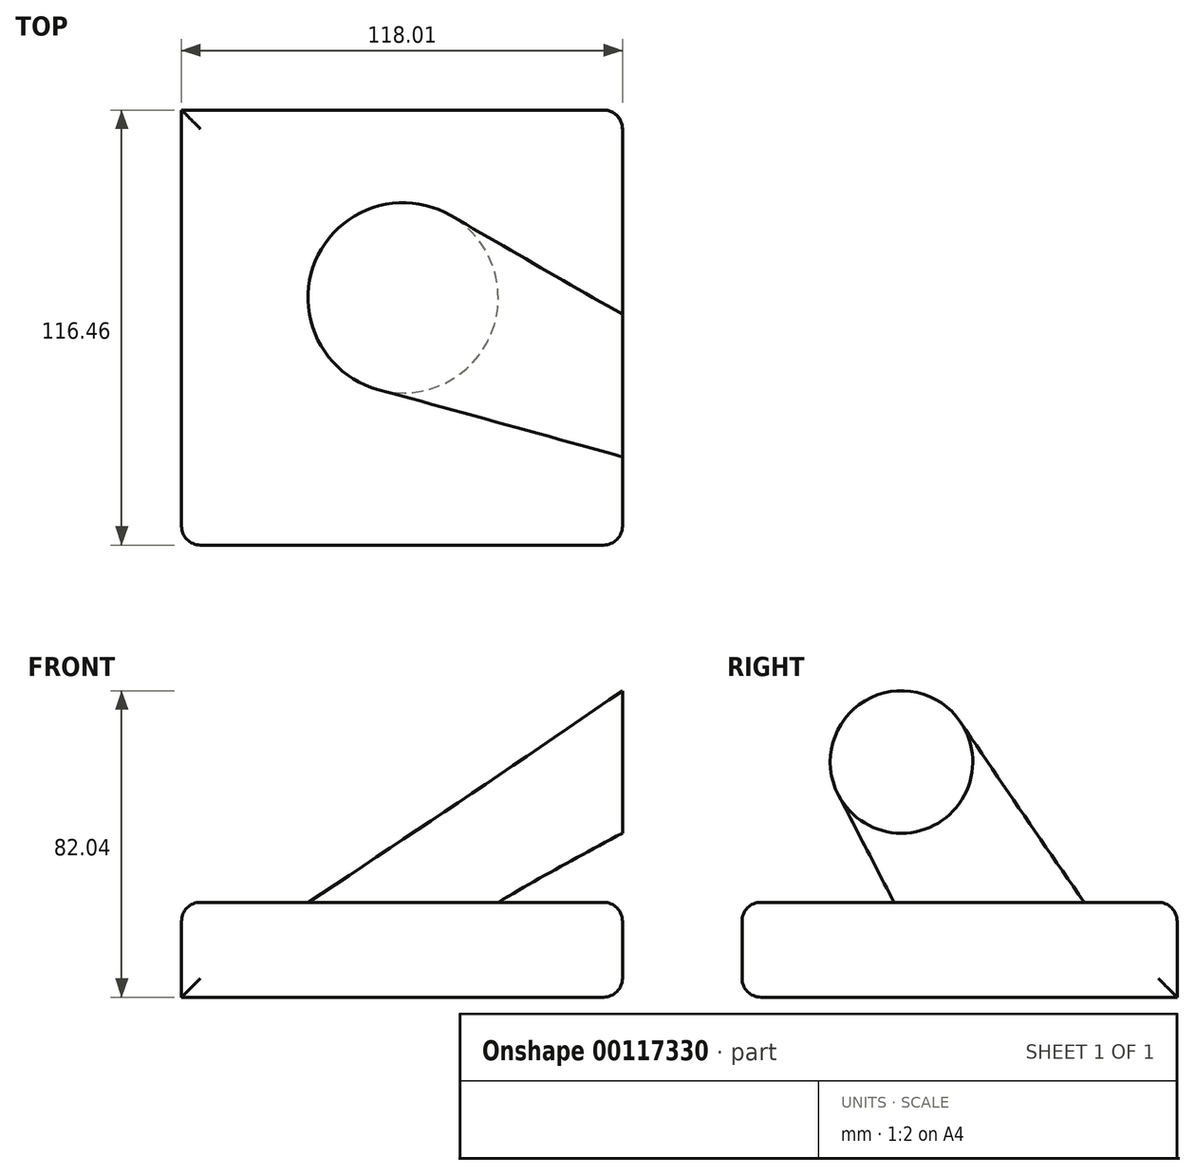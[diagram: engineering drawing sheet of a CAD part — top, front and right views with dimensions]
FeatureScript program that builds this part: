
annotation { "Feature Type Name" : "Feature", "Feature Type Description" : "" }
export const myFeature = defineFeature(function(context is Context, id is Id, definition is map)
    precondition{}
    {
        {
            var Q0;
            Q0=qCreatedBy(makeId("Top.planeOp"),FACE);
            var sketch = newSketch(context, id + "F0", { "sketchPlane" : qUnion([Q0])});
            skLineSegment(sketch, "E0.bottom", {"start": v(-59.31, -66.17) * mm, "end": v(58.7, -66.17) * mm});
            skLineSegment(sketch, "E0.top", {"start": v(-59.31, 50.29) * mm, "end": v(58.7, 50.29) * mm});
            skLineSegment(sketch, "E0.left", {"start": v(-59.31, -66.17) * mm, "end": v(-59.31, 50.29) * mm});
            skLineSegment(sketch, "E0.right", {"start": v(58.7, -66.17) * mm, "end": v(58.7, 50.29) * mm});
            skSolve(sketch);
        }
        {
            var Q0;
            Q0 = qSketchRegion(id + "F0", true);
            extrude(context, id + "F1", {"entities" : qUnion([Q0]), "depth" : 25.4 * mm});
        }
        {
            var Q0;
            Q0=makeQuery(id+"F1.opExtrude","CAP_EDGE",EDGE,{"disambiguationData":[OSD([sQuery(id+"F0.wireOp",EDGE,"E0.bottom")])],"isStart":false});
            var Q1;
            Q1=makeQuery(id+"F1.opExtrude","CAP_EDGE",EDGE,{"disambiguationData":[OSD([sQuery(id+"F0.wireOp",EDGE,"E0.left")])],"isStart":false});
            var Q2;
            Q2=makeQuery(id+"F1.opExtrude","SWEPT_FACE",FACE,{"disambiguationData":[OSD([sQuery(id+"F0.wireOp",EDGE,"E0.right")])]});
            var Q3;
            Q3=makeQuery(id+"F1.opExtrude","SWEPT_FACE",FACE,{"disambiguationData":[OSD([sQuery(id+"F0.wireOp",EDGE,"E0.bottom")])]});
            var Q4;
            Q4=makeQuery(id+"F1.opExtrude","CAP_FACE",FACE,{"disambiguationData":[OSD([sQuery(id+"F0.wireOp",EDGE,"E0.bottom"),sQuery(id+"F0.wireOp",EDGE,"E0.top"),sQuery(id+"F0.wireOp",EDGE,"E0.left"),sQuery(id+"F0.wireOp",EDGE,"E0.right")])],"isStart":false});
            fillet(context, id + "F2", {"entities" : qUnion([Q0, Q1, Q2, Q3, Q4]), "radius" : 5.08 * mm, "tangentPropagation" : true, "allowEdgeOverflow" : false});
        }
        {
            var Q0;
            Q0=makeQuery(id+"F1.opExtrude","CAP_FACE",FACE,{"disambiguationData":[OSD([sQuery(id+"F0.wireOp",EDGE,"E0.bottom"),sQuery(id+"F0.wireOp",EDGE,"E0.top"),sQuery(id+"F0.wireOp",EDGE,"E0.left"),sQuery(id+"F0.wireOp",EDGE,"E0.right")])],"isStart":false});
            var sketch = newSketch(context, id + "F3", { "sketchPlane" : qUnion([Q0])});
            skCircle(sketch, "E1", {"center": v(0, 0) * mm, "radius": 25.45 * mm});
            skSolve(sketch);
        }
        {
            var Q0;
            Q0=makeQuery(id+"F1.opExtrude","SWEPT_FACE",FACE,{"disambiguationData":[OSD([sQuery(id+"F0.wireOp",EDGE,"E0.right")])]});
            cPlane(context, id + "F4", {"entities" : qUnion([Q0]), "cplaneType" : CPlaneType.OFFSET, "offset" : 0 * mm, "width" : 152.4 * mm, "height" : 152.4 * mm});
        }
        {
            var Q0;
            Q0=qCreatedBy(id+"F4.planeOp",FACE);
            var sketch = newSketch(context, id + "F5", { "sketchPlane" : qUnion([Q0])});
            skCircle(sketch, "E2", {"center": v(-23.48, 62.96) * mm, "radius": 19.07 * mm});
            skSolve(sketch);
        }
        {
            var Q1;
            Q1=makeQuery(id+"F5.imprint","IMPRINT",FACE,{"disambiguationData":[TD([[makeQuery(id+"F5.imprint","IMPRINT",EDGE,{"derivedFrom":sQuery(id+"F5.wireOp",EDGE,"E2")}),1.0]])]});
            var Q2;
            Q2=makeQuery(id+"F3.imprint","IMPRINT",FACE,{"disambiguationData":[TD([[makeQuery(id+"F3.imprint","IMPRINT",EDGE,{"derivedFrom":sQuery(id+"F3.wireOp",EDGE,"E1")}),1.0]])]});
            loft(context, id + "F6", {"operationType" : NewBodyOperationType.ADD, "sheetProfilesArray" : [{ "sheetProfileEntities" : qUnion([Q1]) }, { "sheetProfileEntities" : qUnion([Q2]) }]});
        }
    });
